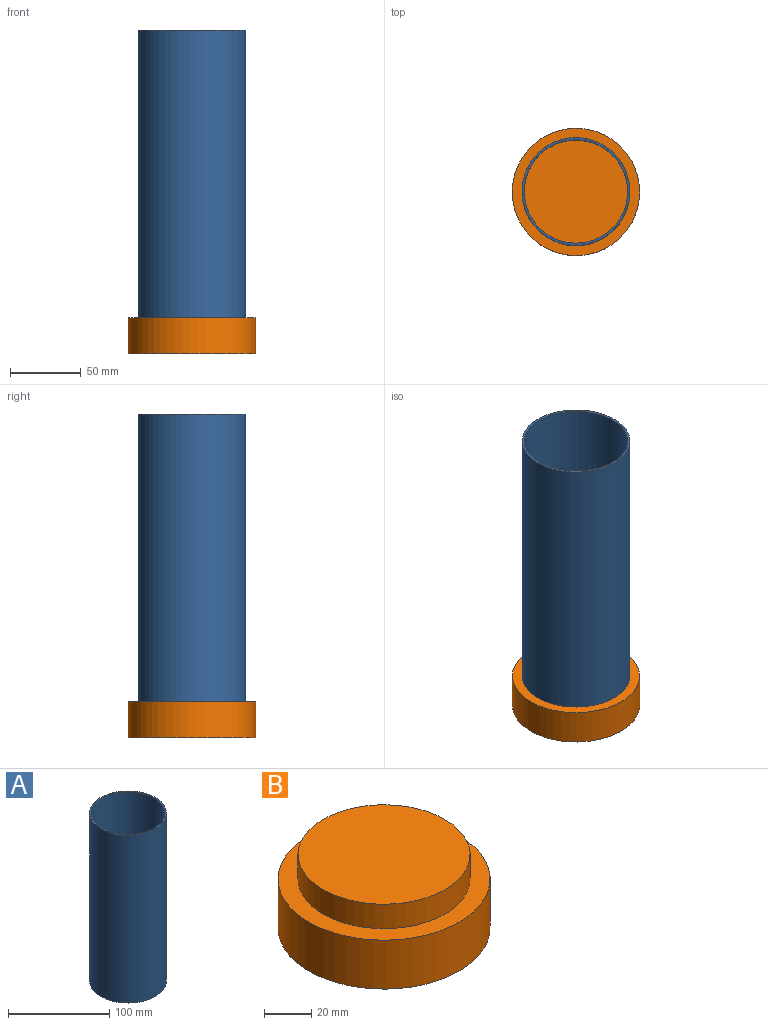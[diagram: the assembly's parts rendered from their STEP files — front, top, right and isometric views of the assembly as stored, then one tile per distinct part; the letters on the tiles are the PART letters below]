
ASSEMBLY  parts=2 mates=1
PART A: 4 faces, bbox 76.2x76.2x203.2 mm
  f0: cylinder r=36.51mm len=203.2mm, axis (0,0,-1), area 46617.1mm2, adj f2,f3
  f1: cylinder r=38.1mm len=203.2mm, axis (0,0,-1), area 48643.9mm2, adj f2,f3
  f2: plane 76.2x76.2mm, normal (0,0,1), area 372.1mm2, adj f0,f1
  f3: plane 76.2x76.2mm, normal (0,0,-1), area 372.1mm2, adj f0,f1
PART B: 7 faces, bbox 90x90x38.1 mm
  f0: cylinder r=44.99mm len=89.98mm, axis (0,0,1), area 7180.1mm2, adj f1,f2
  f1: plane 89.98x89.98mm, normal (0,0,-1), area 6232.3mm2, adj f0,f5
  f2: plane 89.98x89.98mm, normal (0,0,1), area 2170.7mm2, adj f0,f3
  f3: cylinder r=36.51mm len=73.03mm, axis (0,0,-1), area 2913.6mm2, adj f2,f4
  f4: plane 73.03x73.03mm, normal (0,0,1), area 4188.3mm2, adj f3
  f5: cylinder r=6.35mm len=19.05mm, axis (0,0,-1), area 760.1mm2, adj f1,f6
  f6: plane 12.7x12.7mm, normal (0,0,-1), area 126.7mm2, adj f5
PLACE A at identity
PLACE B at identity
MATE fastened A.f0 <-> B.f0  axis (0,0,-1) through (0,0,0)mm
